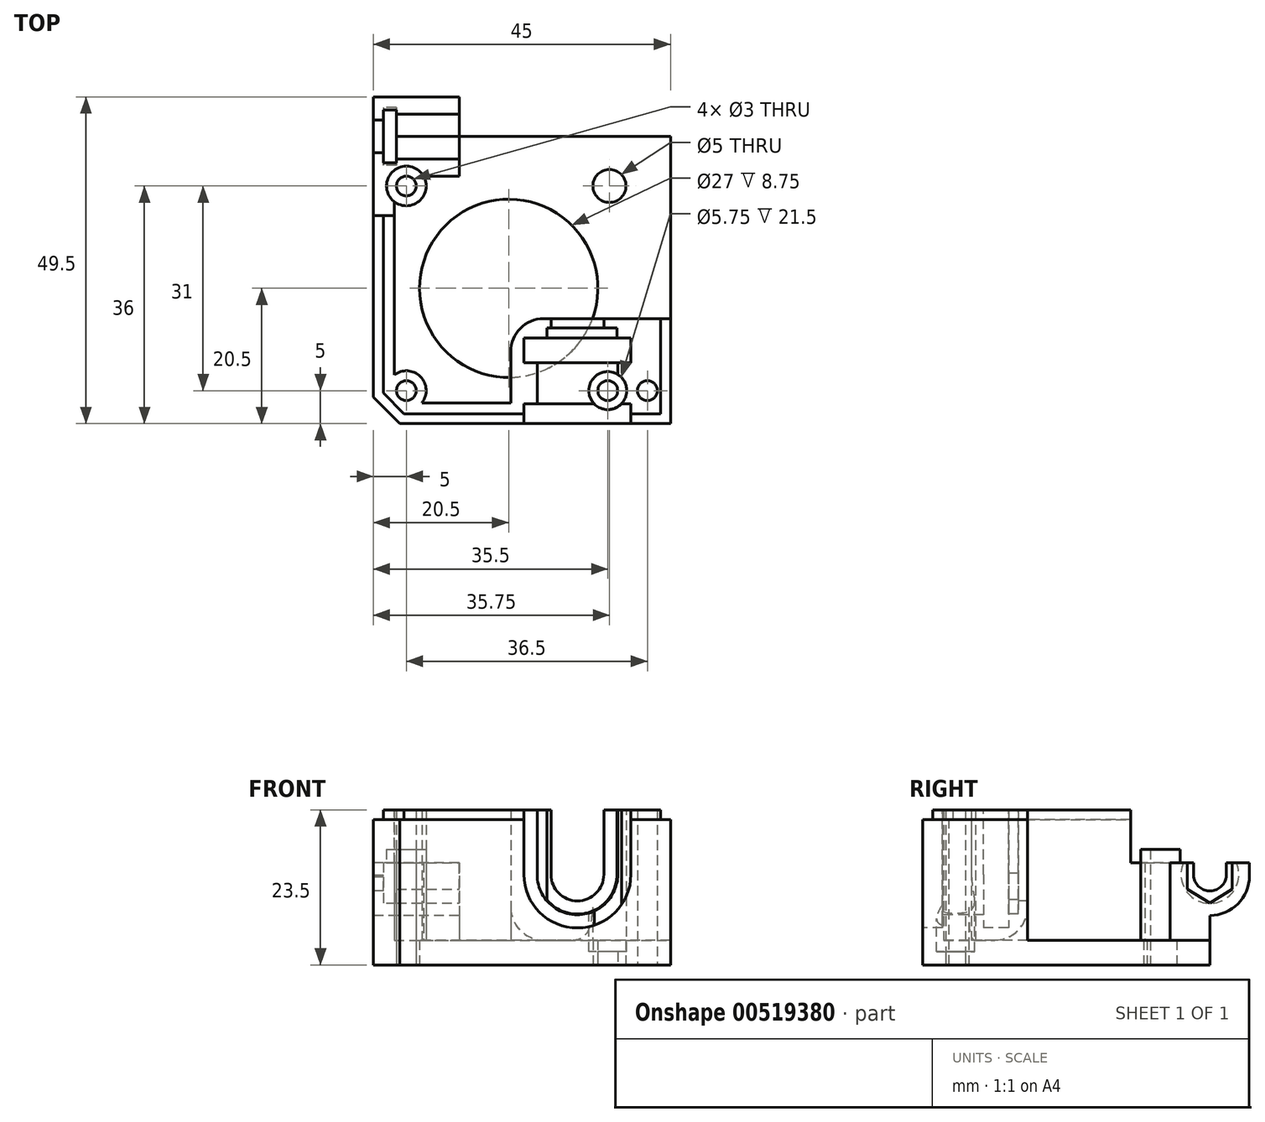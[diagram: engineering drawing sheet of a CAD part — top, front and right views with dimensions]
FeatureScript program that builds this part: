
annotation { "Feature Type Name" : "Feature", "Feature Type Description" : "" }
export const myFeature = defineFeature(function(context is Context, id is Id, definition is map)
    precondition{}
    {
        {
            var Q0;
            Q0=qCreatedBy(makeId("Top.planeOp"),FACE);
            var sketch = newSketch(context, id + "F0", { "sketchPlane" : qUnion([Q0])});
            skLineSegment(sketch, "E0.bottom", {"start": v(0, 0) * mm, "end": v(45, 0) * mm});
            skLineSegment(sketch, "E0.top", {"start": v(0, 43.5) * mm, "end": v(45, 43.5) * mm});
            skLineSegment(sketch, "E0.left", {"start": v(0, 0) * mm, "end": v(0, 43.5) * mm});
            skLineSegment(sketch, "E0.right", {"start": v(45, 0) * mm, "end": v(45, 43.5) * mm});
            skCircle(sketch, "E1", {"center": v(35.75, 36) * mm, "radius": 2.5 * mm});
            skCircle(sketch, "E2", {"center": v(5, 36) * mm, "radius": 1.5 * mm});
            skCircle(sketch, "E3", {"center": v(5, 5) * mm, "radius": 1.5 * mm});
            skCircle(sketch, "E4", {"center": v(35.5, 5) * mm, "radius": 1.5 * mm});
            skCircle(sketch, "E5", {"center": v(41.5, 5) * mm, "radius": 1.5 * mm});
            skCircle(sketch, "E6", {"center": v(20.5, 20.5) * mm, "radius": 13.5 * mm});
            skSolve(sketch);
        }
        {
            var Q0;
            Q0=makeQuery(id+"F0.imprint","IMPRINT",FACE,{"disambiguationData":[TD([[makeQuery(id+"F0.imprint","IMPRINT",EDGE,{"derivedFrom":sQuery(id+"F0.wireOp",EDGE,"E0.bottom")}),1.0]])]});
            extrude(context, id + "F1", {"entities" : qUnion([Q0]), "depth" : 3.75 * mm, "offsetDistance" : 25 * mm});
        }
        {
            var Q0;
            Q0=makeQuery(id+"F1.opExtrude","CAP_FACE",FACE,{"disambiguationData":[OSD([sQuery(id+"F0.wireOp",EDGE,"E0.bottom"),sQuery(id+"F0.wireOp",EDGE,"E0.top"),sQuery(id+"F0.wireOp",EDGE,"E0.left"),sQuery(id+"F0.wireOp",EDGE,"E0.right"),sQuery(id+"F0.wireOp",EDGE,"E1"),sQuery(id+"F0.wireOp",EDGE,"E2"),sQuery(id+"F0.wireOp",EDGE,"E3"),sQuery(id+"F0.wireOp",EDGE,"E4"),sQuery(id+"F0.wireOp",EDGE,"E5"),sQuery(id+"F0.wireOp",EDGE,"E6")])],"isStart":false});
            var sketch = newSketch(context, id + "F2", { "sketchPlane" : qUnion([Q0])});
            skLineSegment(sketch, "E7.0.1", {"start": v(0, 43.5) * mm, "end": v(0, 0) * mm});
            skCircle(sketch, "E8", {"center": v(41.5, 5) * mm, "radius": 1.5 * mm});
            skCircle(sketch, "E9", {"center": v(35.5, 5) * mm, "radius": 1.5 * mm});
            skCircle(sketch, "E10", {"center": v(5, 5) * mm, "radius": 1.5 * mm});
            skCircle(sketch, "E11", {"center": v(5, 36) * mm, "radius": 1.5 * mm});
            skLineSegment(sketch, "E12", {"start": v(0, 43.5) * mm, "end": v(13, 43.5) * mm});
            skLineSegment(sketch, "E13", {"start": v(0, 0) * mm, "end": v(0, 43.5) * mm});
            skLineSegment(sketch, "E14", {"start": v(0, 0) * mm, "end": v(45, 0) * mm});
            skLineSegment(sketch, "E15", {"start": v(45, 0) * mm, "end": v(45, 15.9) * mm});
            skArc(sketch, "E16", {"start": v(3.15, 33.64) * mm, "mid": v(6.97, 33.73) * mm, "end": v(7.6, 37.5) * mm});
            skLineSegment(sketch, "E17", {"start": v(13, 37.5) * mm, "end": v(13, 43.5) * mm});
            skLineSegment(sketch, "E18", {"start": v(7.36, 3.15) * mm, "end": v(20.8, 3.15) * mm});
            skLineSegment(sketch, "E19", {"start": v(45, 15.9) * mm, "end": v(20.8, 15.9) * mm});
            skLineSegment(sketch, "E20", {"start": v(20.8, 15.9) * mm, "end": v(20.8, 3.15) * mm});
            skPoint(sketch, "E21.orphan", {"position": v(45, 43.5) * mm});
            skLineSegment(sketch, "E22.trimOffspring", {"start": v(7.6, 37.5) * mm, "end": v(13, 37.5) * mm});
            skLineSegment(sketch, "E23.trimOffspring", {"start": v(3.15, 33.64) * mm, "end": v(3.15, 7.36) * mm});
            skArc(sketch, "E24.trimOffspring", {"start": v(7.36, 3.15) * mm, "mid": v(7.12, 7.12) * mm, "end": v(3.15, 7.36) * mm});
            skPoint(sketch, "E7.0.2.end.orphan", {"position": v(45, 0) * mm});
            skSolve(sketch);
        }
        {
            var Q0;
            Q0 = qSketchRegion(id + "F2", true);
            extrude(context, id + "F3", {"entities" : qUnion([Q0]), "operationType" : NewBodyOperationType.ADD, "depth" : (23.5 - 3.75) * mm, "offsetDistance" : 25 * mm});
        }
        {
            var Q0;
            Q0=makeQuery(id+"F3.boolean.opBoolean","MERGE",EDGE,{"derivedFrom":[makeQuery(id+"F1.opExtrude","SWEPT_EDGE",EDGE,{"disambiguationData":[OSD([sQuery(id+"F0.wireOp",EDGE,"E0.bottom"),sQuery(id+"F0.wireOp",EDGE,"E0.left")])]}),makeQuery(id+"F3.opExtrude","SWEPT_EDGE",EDGE,{"disambiguationData":[OSD([sQuery(id+"F2.wireOp",EDGE,"E13"),sQuery(id+"F2.wireOp",EDGE,"E14")])]})]});
            chamfer(context, id + "F4", {"entities" : qUnion([Q0]), "width" : 4 * mm, "tangentPropagation" : true});
        }
        {
            var Q0;
            Q0=makeQuery(id+"F3.boolean.opBoolean","MERGE",FACE,{"derivedFrom":[makeQuery(id+"F1.opExtrude","SWEPT_FACE",FACE,{"disambiguationData":[OSD([sQuery(id+"F0.wireOp",EDGE,"E0.left")])]}),makeQuery(id+"F3.opExtrude","SWEPT_FACE",FACE,{"disambiguationData":[OSD([sQuery(id+"F2.wireOp",EDGE,"E13")])]})]});
            var sketch = newSketch(context, id + "F5", { "sketchPlane" : qUnion([Q0])});
            skLineSegment(sketch, "E25.bottom", {"start": v(-43.5, 23.5) * mm, "end": v(-31.5, 23.5) * mm});
            skLineSegment(sketch, "E25.top", {"start": v(-43.5, 15.5) * mm, "end": v(-31.5, 15.5) * mm});
            skLineSegment(sketch, "E25.left", {"start": v(-43.5, 23.5) * mm, "end": v(-43.5, 15.5) * mm});
            skLineSegment(sketch, "E25.right", {"start": v(-31.5, 23.5) * mm, "end": v(-31.5, 15.5) * mm});
            skSolve(sketch);
        }
        {
            var Q0;
            Q0=makeQuery(id+"F5.imprint","IMPRINT",FACE,{"disambiguationData":[TD([[makeQuery(id+"F5.imprint","IMPRINT",EDGE,{"derivedFrom":sQuery(id+"F5.wireOp",EDGE,"E25.bottom")}),1.0]])]});
            extrude(context, id + "F6", {"entities" : qUnion([Q0]), "operationType" : NewBodyOperationType.REMOVE, "endBound" : BoundingType.THROUGH_ALL, "oppositeDirection" : true, "depth" : 25 * mm, "offsetDistance" : 25 * mm});
        }
        {
            var Q0;
            Q0=makeQuery(id+"F3.boolean.opBoolean","MERGE",FACE,{"derivedFrom":[makeQuery(id+"F1.opExtrude","SWEPT_FACE",FACE,{"disambiguationData":[OSD([sQuery(id+"F0.wireOp",EDGE,"E0.left")])]}),makeQuery(id+"F3.opExtrude","SWEPT_FACE",FACE,{"disambiguationData":[OSD([sQuery(id+"F2.wireOp",EDGE,"E13")])]})]});
            var sketch = newSketch(context, id + "F7", { "sketchPlane" : qUnion([Q0])});
            skArc(sketch, "E26", {"start": v(-49.5, 13.5) * mm, "mid": v(-47.74, 9.26) * mm, "end": v(-43.5, 7.5) * mm});
            skLineSegment(sketch, "E27", {"start": v(-49.5, 13.5) * mm, "end": v(-49.5, 15.5) * mm});
            skLineSegment(sketch, "E28", {"start": v(-43.5, 15.5) * mm, "end": v(-49.5, 15.5) * mm});
            skLineSegment(sketch, "E29.bottom", {"start": v(-43.5, 15.5) * mm, "end": v(-40.04, 15.5) * mm});
            skLineSegment(sketch, "E29.top", {"start": v(-43.5, 7.5) * mm, "end": v(-40.04, 7.5) * mm});
            skLineSegment(sketch, "E29.right", {"start": v(-40.04, 15.5) * mm, "end": v(-40.04, 7.5) * mm});
            skSolve(sketch);
        }
        {
            var Q0;
            Q0 = qSketchRegion(id + "F7", true);
            var Q1;
            Q1=makeQuery(id+"F3.opExtrude","SWEPT_FACE",FACE,{"disambiguationData":[OSD([sQuery(id+"F2.wireOp",EDGE,"E17")])]});
            extrude(context, id + "F8", {"entities" : qUnion([Q0]), "operationType" : NewBodyOperationType.ADD, "endBound" : BoundingType.UP_TO_SURFACE, "oppositeDirection" : true, "depth" : 25 * mm, "endBoundEntityFace" : qUnion([Q1]), "offsetDistance" : 25 * mm});
        }
        {
            var Q0;
            Q0=makeQuery(id+"F8.boolean.opBoolean","MERGE",FACE,{"derivedFrom":[makeQuery(id+"F3.boolean.opBoolean","MERGE",FACE,{"derivedFrom":[makeQuery(id+"F1.opExtrude","SWEPT_FACE",FACE,{"disambiguationData":[OSD([sQuery(id+"F0.wireOp",EDGE,"E0.left")])]}),makeQuery(id+"F3.opExtrude","SWEPT_FACE",FACE,{"disambiguationData":[OSD([sQuery(id+"F2.wireOp",EDGE,"E13")])]})]}),makeQuery(id+"F8.opExtrude","CAP_FACE",FACE,{"disambiguationData":[OSD([sQuery(id+"F7.wireOp",EDGE,"E26"),sQuery(id+"F7.wireOp",EDGE,"E27"),sQuery(id+"F7.wireOp",EDGE,"E28"),sQuery(id+"F7.wireOp",EDGE,"E29.bottom"),sQuery(id+"F7.wireOp",EDGE,"E29.top"),sQuery(id+"F7.wireOp",EDGE,"E29.right")])],"isStart":true})]});
            var sketch = newSketch(context, id + "F9", { "sketchPlane" : qUnion([Q0])});
            skArc(sketch, "E30", {"start": v(-46, 13.85) * mm, "mid": v(-43.4, 11.2) * mm, "end": v(-41.03, 14.07) * mm});
            skLineSegment(sketch, "E31", {"start": v(-46, 15.5) * mm, "end": v(-46, 13.55) * mm});
            skLineSegment(sketch, "E32", {"start": v(-41.03, 15.5) * mm, "end": v(-41.03, 13.33) * mm});
            skLineSegment(sketch, "E33", {"start": v(-46, 15.5) * mm, "end": v(-41.03, 15.5) * mm});
            skSolve(sketch);
        }
        {
            var Q0;
            {var subQ3=sQuery(id+"F9.wireOp",EDGE,"E33");Q0=makeQuery(id+"F9.imprint","IMPRINT",FACE,{"disambiguationData":[TD([[makeQuery(id+"F9.imprint","IMPRINT",EDGE,{"derivedFrom":subQ3}),-1.0]])]});}
            extrude(context, id + "F10", {"entities" : qUnion([Q0]), "operationType" : NewBodyOperationType.REMOVE, "endBound" : BoundingType.THROUGH_ALL, "oppositeDirection" : true, "depth" : 25 * mm, "offsetDistance" : 25 * mm});
        }
        {
            var Q0;
            {var subQ1=sQuery(id+"F7.wireOp",EDGE,"E29.bottom");var subQ2=sQuery(id+"F7.wireOp",EDGE,"E28");Q0=makeQuery(id+"F10.boolean.opBoolean","SPLIT",FACE,{"disambiguationData":[TD([makeQuery(id+"F1.opExtrude","SWEPT_FACE",FACE,{"disambiguationData":[OSD([sQuery(id+"F0.wireOp",EDGE,"E2")])]})])],"derivedFrom":makeQuery(id+"F8.boolean.opBoolean","MERGE",FACE,{"derivedFrom":[makeQuery(id+"F6.boolean.opBoolean","COPY",FACE,{"derivedFrom":makeQuery(id+"F6.opExtrude","SWEPT_FACE",FACE,{"disambiguationData":[OSD([sQuery(id+"F5.wireOp",EDGE,"E25.top")])]})}),makeQuery(id+"F8.opExtrude","SWEPT_FACE",FACE,{"disambiguationData":[OSD([subQ2,subQ1])]})]})});}
            var sketch = newSketch(context, id + "F11", { "sketchPlane" : qUnion([Q0])});
            skCircle(sketch, "E34.0", {"center": v(5, 36) * mm, "radius": 1.5 * mm});
            skCircle(sketch, "E35", {"center": v(5, 36) * mm, "radius": 3 * mm});
            skSolve(sketch);
        }
        {
            var Q0;
            Q0 = qSketchRegion(id + "F11", true);
            extrude(context, id + "F12", {"entities" : qUnion([Q0]), "operationType" : NewBodyOperationType.ADD, "depth" : 2 * mm, "offsetDistance" : 25 * mm});
        }
        {
            var Q0;
            {var subQ0=sQuery(id+"F2.wireOp",EDGE,"E17");Q0=makeQuery(id+"F8.boolean.opBoolean","MERGE",FACE,{"derivedFrom":[makeQuery(id+"F3.opExtrude","SWEPT_FACE",FACE,{"disambiguationData":[OSD([subQ0])]}),makeQuery(id+"F8.opExtrude","CAP_FACE",FACE,{"disambiguationData":[OSD([subQ0])],"isStart":false})]});}
            var sketch = newSketch(context, id + "F13", { "sketchPlane" : qUnion([Q0])});
            skLineSegment(sketch, "E36", {"start": v(40.1, 15.5) * mm, "end": v(40.1, 11.5) * mm});
            skLineSegment(sketch, "E37", {"start": v(40.1, 11.5) * mm, "end": v(43.5, 9.4) * mm});
            skLineSegment(sketch, "E38", {"start": v(43.5, 9.4) * mm, "end": v(46.9, 11.5) * mm});
            skLineSegment(sketch, "E39", {"start": v(46.9, 11.5) * mm, "end": v(46.9, 15.5) * mm});
            skLineSegment(sketch, "E40", {"start": v(46.9, 15.5) * mm, "end": v(40.1, 15.5) * mm});
            skSolve(sketch);
        }
        {
            var Q0;
            Q0 = qSketchRegion(id + "F13", true);
            extrude(context, id + "F14", {"entities" : qUnion([Q0]), "operationType" : NewBodyOperationType.REMOVE, "oppositeDirection" : true, "depth" : 11.5 * mm, "offsetDistance" : 25 * mm});
        }
        {
            var Q0;
            Q0=makeQuery(id+"F14.boolean.opBoolean","COPY",FACE,{"derivedFrom":makeQuery(id+"F14.opExtrude","CAP_FACE",FACE,{"disambiguationData":[OSD([sQuery(id+"F13.wireOp",EDGE,"E36"),sQuery(id+"F13.wireOp",EDGE,"E37"),sQuery(id+"F13.wireOp",EDGE,"E38"),sQuery(id+"F13.wireOp",EDGE,"E39"),sQuery(id+"F13.wireOp",EDGE,"E40")])],"isStart":false})});
            var sketch = newSketch(context, id + "F15", { "sketchPlane" : qUnion([Q0])});
            skCircle(sketch, "E41", {"center": v(43.5, 13.7) * mm, "radius": 4.38 * mm});
            skSolve(sketch);
        }
        {
            var Q0;
            Q0 = qSketchRegion(id + "F15", true);
            extrude(context, id + "F16", {"entities" : qUnion([Q0]), "operationType" : NewBodyOperationType.REMOVE, "depth" : 2 * mm, "offsetDistance" : 25 * mm});
        }
        {
            var Q0;
            Q0=makeQuery(id+"F3.opExtrude","CAP_FACE",FACE,{"disambiguationData":[OSD([sQuery(id+"F2.wireOp",EDGE,"E8"),sQuery(id+"F2.wireOp",EDGE,"E9"),sQuery(id+"F2.wireOp",EDGE,"E10"),sQuery(id+"F2.wireOp",EDGE,"E11"),sQuery(id+"F2.wireOp",EDGE,"E12"),sQuery(id+"F2.wireOp",EDGE,"E13"),sQuery(id+"F2.wireOp",EDGE,"E14"),sQuery(id+"F2.wireOp",EDGE,"E15"),sQuery(id+"F2.wireOp",EDGE,"E16"),sQuery(id+"F2.wireOp",EDGE,"E17"),sQuery(id+"F2.wireOp",EDGE,"E18"),sQuery(id+"F2.wireOp",EDGE,"E19"),sQuery(id+"F2.wireOp",EDGE,"E20"),sQuery(id+"F2.wireOp",EDGE,"E22.trimOffspring"),sQuery(id+"F2.wireOp",EDGE,"E23.trimOffspring"),sQuery(id+"F2.wireOp",EDGE,"E24.trimOffspring")])],"isStart":false});
            var sketch = newSketch(context, id + "F17", { "sketchPlane" : qUnion([Q0])});
            skLineSegment(sketch, "E42", {"start": v(1.5, 31.5) * mm, "end": v(0, 31.5) * mm});
            skLineSegment(sketch, "E43", {"start": v(0, 4) * mm, "end": v(0, 31.5) * mm});
            skLineSegment(sketch, "E44", {"start": v(0, 4) * mm, "end": v(4, 0) * mm});
            skLineSegment(sketch, "E45", {"start": v(4, 0) * mm, "end": v(45, 0) * mm});
            skLineSegment(sketch, "E46", {"start": v(45, 0) * mm, "end": v(45, 15.9) * mm});
            skLineSegment(sketch, "E47", {"start": v(45, 15.9) * mm, "end": v(43.5, 15.9) * mm});
            skLineSegment(sketch, "E48", {"start": v(1.5, 31.5) * mm, "end": v(1.5, 4.62) * mm});
            skLineSegment(sketch, "E49", {"start": v(1.5, 4.62) * mm, "end": v(4.62, 1.5) * mm});
            skLineSegment(sketch, "E50", {"start": v(4.62, 1.5) * mm, "end": v(43.5, 1.5) * mm});
            skLineSegment(sketch, "E51", {"start": v(43.5, 1.5) * mm, "end": v(43.5, 15.9) * mm});
            skSolve(sketch);
        }
        {
            var Q0;
            Q0 = qSketchRegion(id + "F17", true);
            extrude(context, id + "F18", {"entities" : qUnion([Q0]), "operationType" : NewBodyOperationType.REMOVE, "oppositeDirection" : true, "depth" : 1.5 * mm, "offsetDistance" : 25 * mm});
        }
        {
            var Q0;
            Q0=makeQuery(id+"F3.boolean.opBoolean","MERGE",FACE,{"derivedFrom":[makeQuery(id+"F1.opExtrude","SWEPT_FACE",FACE,{"disambiguationData":[OSD([sQuery(id+"F0.wireOp",EDGE,"E0.bottom")])]}),makeQuery(id+"F3.opExtrude","SWEPT_FACE",FACE,{"disambiguationData":[OSD([sQuery(id+"F2.wireOp",EDGE,"E14")])]})]});
            var sketch = newSketch(context, id + "F19", { "sketchPlane" : qUnion([Q0])});
            skArc(sketch, "E52", {"start": v(22.8, 13.7) * mm, "mid": v(30.9, 5.6) * mm, "end": v(39, 13.7) * mm});
            skLineSegment(sketch, "E53", {"start": v(22.8, 13.7) * mm, "end": v(22.8, 23.94) * mm});
            skLineSegment(sketch, "E54", {"start": v(22.8, 23.94) * mm, "end": v(39, 23.94) * mm});
            skLineSegment(sketch, "E55", {"start": v(39, 23.94) * mm, "end": v(39, 13.7) * mm});
            skSolve(sketch);
        }
        {
            var Q0;
            {var subQ2=sQuery(id+"F19.wireOp",EDGE,"E52");Q0=makeQuery(id+"F19.imprint","IMPRINT",FACE,{"disambiguationData":[TD([[makeQuery(id+"F19.imprint","IMPRINT",EDGE,{"derivedFrom":subQ2}),-1.0]])]});}
            var sketch = newSketch(context, id + "F20", { "sketchPlane" : qUnion([Q0])});
            skArc(sketch, "E56", {"start": v(26.9, 13.7) * mm, "mid": v(30.9, 9.7) * mm, "end": v(34.9, 13.7) * mm});
            skLineSegment(sketch, "E57", {"start": v(26.9, 13.7) * mm, "end": v(26.9, 27) * mm});
            skLineSegment(sketch, "E58", {"start": v(26.9, 27) * mm, "end": v(34.9, 27) * mm});
            skLineSegment(sketch, "E59", {"start": v(34.9, 27) * mm, "end": v(34.9, 13.7) * mm});
            skSolve(sketch);
        }
        {
            var Q0;
            Q0 = qSketchRegion(id + "F20", true);
            extrude(context, id + "F21", {"entities" : qUnion([Q0]), "operationType" : NewBodyOperationType.REMOVE, "endBound" : BoundingType.THROUGH_ALL, "oppositeDirection" : true, "depth" : 25 * mm, "offsetDistance" : 25 * mm});
        }
        {
            var Q0;
            Q0 = qSketchRegion(id + "F19", true);
            extrude(context, id + "F22", {"entities" : qUnion([Q0]), "operationType" : NewBodyOperationType.REMOVE, "oppositeDirection" : true, "depth" : (16 - 3) * mm, "offsetDistance" : 25 * mm, "hasSecondDirection" : true, "secondDirectionOppositeDirection" : true, "secondDirectionDepth" : (13 - 3.8) * mm});
        }
        {
            var Q0;
            Q0 = qSketchRegion(id + "F19", true);
            extrude(context, id + "F23", {"entities" : qUnion([Q0]), "operationType" : NewBodyOperationType.REMOVE, "oppositeDirection" : true, "depth" : 3 * mm, "offsetDistance" : 25 * mm});
        }
        {
            var Q0;
            Q0=makeQuery(id+"F3.opExtrude","SWEPT_EDGE",EDGE,{"disambiguationData":[OSD([sQuery(id+"F2.wireOp",EDGE,"E19"),sQuery(id+"F2.wireOp",EDGE,"E20")])]});
            var Q1;
            {var subQ0=sQuery(id+"F2.wireOp",EDGE,"E19");Q1=makeQuery(id+"F3.boolean.opBoolean","SPLIT",EDGE,{"disambiguationData":[topologyDisambiguationEdgeConnected([makeQuery(id+"F3.opExtrude","CAP_FACE",FACE,{"disambiguationData":[OSD([sQuery(id+"F2.wireOp",EDGE,"E8"),sQuery(id+"F2.wireOp",EDGE,"E9"),sQuery(id+"F2.wireOp",EDGE,"E10"),sQuery(id+"F2.wireOp",EDGE,"E11"),sQuery(id+"F2.wireOp",EDGE,"E12"),sQuery(id+"F2.wireOp",EDGE,"E13"),sQuery(id+"F2.wireOp",EDGE,"E14"),sQuery(id+"F2.wireOp",EDGE,"E15"),sQuery(id+"F2.wireOp",EDGE,"E16"),sQuery(id+"F2.wireOp",EDGE,"E17"),sQuery(id+"F2.wireOp",EDGE,"E18"),subQ0,sQuery(id+"F2.wireOp",EDGE,"E20"),sQuery(id+"F2.wireOp",EDGE,"E22.trimOffspring"),sQuery(id+"F2.wireOp",EDGE,"E23.trimOffspring"),sQuery(id+"F2.wireOp",EDGE,"E24.trimOffspring")])],"isStart":true})])],"derivedFrom":makeQuery(id+"F3.opExtrude","CAP_EDGE",EDGE,{"disambiguationData":[OSD([subQ0])],"isStart":true})});}
            var Q2;
            {var subQ0=sQuery(id+"F2.wireOp",EDGE,"E20");Q2=makeQuery(id+"F3.boolean.opBoolean","SPLIT",EDGE,{"disambiguationData":[topologyDisambiguationEdgeConnected([makeQuery(id+"F3.opExtrude","CAP_FACE",FACE,{"disambiguationData":[OSD([sQuery(id+"F2.wireOp",EDGE,"E8"),sQuery(id+"F2.wireOp",EDGE,"E9"),sQuery(id+"F2.wireOp",EDGE,"E10"),sQuery(id+"F2.wireOp",EDGE,"E11"),sQuery(id+"F2.wireOp",EDGE,"E12"),sQuery(id+"F2.wireOp",EDGE,"E13"),sQuery(id+"F2.wireOp",EDGE,"E14"),sQuery(id+"F2.wireOp",EDGE,"E15"),sQuery(id+"F2.wireOp",EDGE,"E16"),sQuery(id+"F2.wireOp",EDGE,"E17"),sQuery(id+"F2.wireOp",EDGE,"E18"),sQuery(id+"F2.wireOp",EDGE,"E19"),subQ0,sQuery(id+"F2.wireOp",EDGE,"E22.trimOffspring"),sQuery(id+"F2.wireOp",EDGE,"E23.trimOffspring"),sQuery(id+"F2.wireOp",EDGE,"E24.trimOffspring")])],"isStart":true})])],"derivedFrom":makeQuery(id+"F3.opExtrude","CAP_EDGE",EDGE,{"disambiguationData":[OSD([subQ0])],"isStart":true})});}
            fillet(context, id + "F24", {"entities" : qUnion([Q0, Q1, Q2]), "radius" : 5 * mm, "tangentPropagation" : true, "allowEdgeOverflow" : false});
        }
        {
            var Q0;
            Q0=makeQuery(id+"F3.boolean.opBoolean","MERGE",FACE,{"derivedFrom":[makeQuery(id+"F1.opExtrude","SWEPT_FACE",FACE,{"disambiguationData":[OSD([sQuery(id+"F0.wireOp",EDGE,"E0.bottom")])]}),makeQuery(id+"F3.opExtrude","SWEPT_FACE",FACE,{"disambiguationData":[OSD([sQuery(id+"F2.wireOp",EDGE,"E14")])]})]});
            var sketch = newSketch(context, id + "F25", { "sketchPlane" : qUnion([Q0])});
            skArc(sketch, "E60", {"start": v(24.8, 13.7) * mm, "mid": v(30.9, 7.6) * mm, "end": v(37, 13.7) * mm});
            skLineSegment(sketch, "E61", {"start": v(24.8, 13.7) * mm, "end": v(24.8, 24.84) * mm});
            skLineSegment(sketch, "E62", {"start": v(24.8, 24.84) * mm, "end": v(37, 24.84) * mm});
            skLineSegment(sketch, "E63", {"start": v(37, 24.84) * mm, "end": v(37, 13.7) * mm});
            skSolve(sketch);
        }
        {
            var Q0;
            Q0 = qSketchRegion(id + "F25", true);
            var Q1;
            Q1=makeQuery(id+"F22.boolean.opBoolean","COPY",FACE,{"derivedFrom":makeQuery(id+"F22.opExtrude","CAP_FACE",FACE,{"disambiguationData":[OSD([sQuery(id+"F19.wireOp",EDGE,"E52"),sQuery(id+"F19.wireOp",EDGE,"E53"),sQuery(id+"F19.wireOp",EDGE,"E54"),sQuery(id+"F19.wireOp",EDGE,"E55")])],"isStart":true})});
            extrude(context, id + "F26", {"entities" : qUnion([Q0]), "operationType" : NewBodyOperationType.REMOVE, "endBound" : BoundingType.UP_TO_SURFACE, "oppositeDirection" : true, "depth" : 25 * mm, "endBoundEntityFace" : qUnion([Q1]), "offsetDistance" : 25 * mm});
        }
        {
            var Q0;
            {var subQ0=sQuery(id+"F2.wireOp",EDGE,"E9");var subQ1=sQuery(id+"F2.wireOp",EDGE,"E8");var subQ2=sQuery(id+"F2.wireOp",EDGE,"E19");Q0=makeQuery(id+"F21.boolean.opBoolean","SPLIT",FACE,{"disambiguationData":[TD([makeQuery(id+"F1.opExtrude","SWEPT_FACE",FACE,{"disambiguationData":[OSD([sQuery(id+"F0.wireOp",EDGE,"E4")])]})])],"derivedFrom":makeQuery(id+"F3.opExtrude","CAP_FACE",FACE,{"disambiguationData":[OSD([subQ1,subQ0,sQuery(id+"F2.wireOp",EDGE,"E10"),sQuery(id+"F2.wireOp",EDGE,"E11"),sQuery(id+"F2.wireOp",EDGE,"E12"),sQuery(id+"F2.wireOp",EDGE,"E13"),sQuery(id+"F2.wireOp",EDGE,"E14"),sQuery(id+"F2.wireOp",EDGE,"E15"),sQuery(id+"F2.wireOp",EDGE,"E16"),sQuery(id+"F2.wireOp",EDGE,"E17"),sQuery(id+"F2.wireOp",EDGE,"E18"),subQ2,sQuery(id+"F2.wireOp",EDGE,"E20"),sQuery(id+"F2.wireOp",EDGE,"E22.trimOffspring"),sQuery(id+"F2.wireOp",EDGE,"E23.trimOffspring"),sQuery(id+"F2.wireOp",EDGE,"E24.trimOffspring")])],"isStart":false})});}
            var sketch = newSketch(context, id + "F27", { "sketchPlane" : qUnion([Q0])});
            skCircle(sketch, "E64", {"center": v(35.5, 5) * mm, "radius": 2.88 * mm});
            skSolve(sketch);
        }
        {
            var Q0;
            Q0 = qSketchRegion(id + "F27", true);
            extrude(context, id + "F28", {"entities" : qUnion([Q0]), "operationType" : NewBodyOperationType.REMOVE, "oppositeDirection" : true, "depth" : 21.5 * mm, "offsetDistance" : 25 * mm});
        }
        {
            var Q0;
            Q0=makeQuery(id+"F22.boolean.opBoolean","COPY",FACE,{"derivedFrom":makeQuery(id+"F22.opExtrude","CAP_FACE",FACE,{"disambiguationData":[OSD([sQuery(id+"F19.wireOp",EDGE,"E52"),sQuery(id+"F19.wireOp",EDGE,"E53"),sQuery(id+"F19.wireOp",EDGE,"E54"),sQuery(id+"F19.wireOp",EDGE,"E55")])],"isStart":false})});
            var sketch = newSketch(context, id + "F29", { "sketchPlane" : qUnion([Q0])});
            skArc(sketch, "E65", {"start": v(26.3, 9.85) * mm, "mid": v(33.04, 8.1) * mm, "end": v(36.9, 13.9) * mm});
            skLineSegment(sketch, "E66", {"start": v(36.9, 13.9) * mm, "end": v(36.9, 26.1) * mm});
            skLineSegment(sketch, "E67", {"start": v(36.9, 26.1) * mm, "end": v(26.3, 26.1) * mm});
            skLineSegment(sketch, "E68", {"start": v(26.3, 26.1) * mm, "end": v(26.3, 9.85) * mm});
            skSolve(sketch);
        }
        {
            var Q0;
            Q0 = qSketchRegion(id + "F29", true);
            extrude(context, id + "F30", {"entities" : qUnion([Q0]), "operationType" : NewBodyOperationType.REMOVE, "oppositeDirection" : true, "depth" : 1.5 * mm, "offsetDistance" : 25 * mm});
        }
    });
